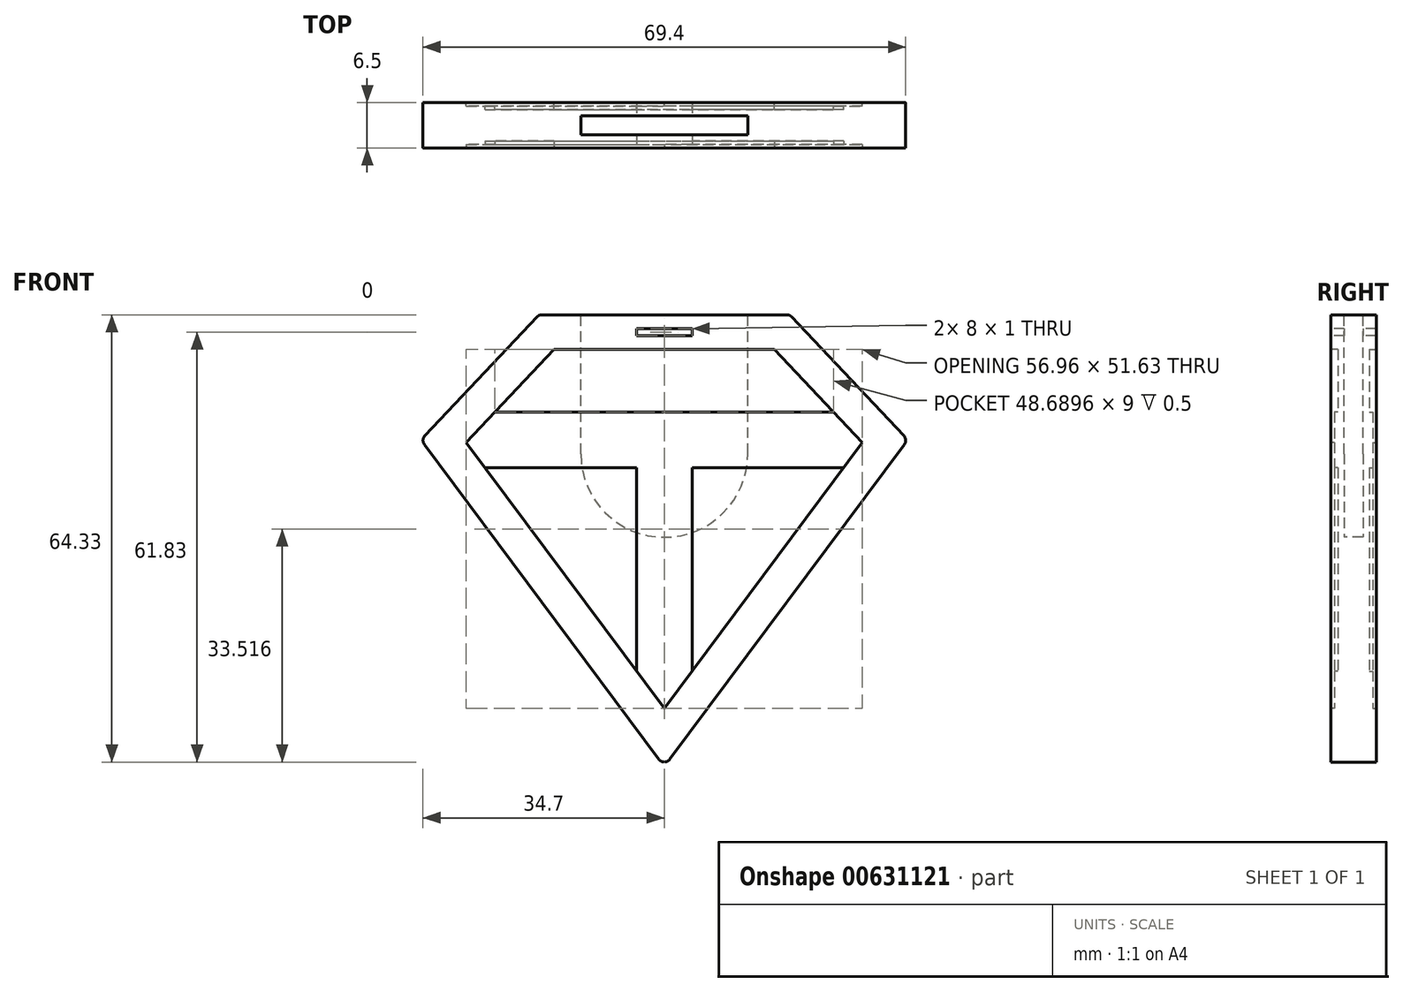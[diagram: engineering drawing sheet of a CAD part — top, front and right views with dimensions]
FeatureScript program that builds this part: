
annotation { "Feature Type Name" : "Feature", "Feature Type Description" : "" }
export const myFeature = defineFeature(function(context is Context, id is Id, definition is map)
    precondition{}
    {
        {
            var Q0;
            Q0=qCreatedBy(makeId("Front.planeOp"),FACE);
            var sketch = newSketch(context, id + "F0", { "sketchPlane" : qUnion([Q0])});
            skLineSegment(sketch, "E0", {"start": v(0, 18) * mm, "end": v(18, 18) * mm});
            skLineSegment(sketch, "E1", {"start": v(18, 18) * mm, "end": v(35, 0) * mm});
            skLineSegment(sketch, "E2", {"start": v(35, 0) * mm, "end": v(0, -47) * mm});
            skLineSegment(sketch, "E3", {"start": v(0, 18) * mm, "end": v(0, -47) * mm, "construction": true});
            skLineSegment(sketch, "E4.MirrorCS", {"start": v(-35, 0) * mm, "end": v(0, -47) * mm});
            skLineSegment(sketch, "E5.MirrorCS", {"start": v(-18, 18) * mm, "end": v(-35, 0) * mm});
            skLineSegment(sketch, "E6.MirrorCS", {"start": v(0, 18) * mm, "end": v(-18, 18) * mm});
            skSolve(sketch);
        }
        {
            var Q0;
            Q0 = qSketchRegion(id + "F0", true);
            extrude(context, id + "F1", {"entities" : qUnion([Q0]), "endBound" : BoundingType.SYMMETRIC, "depth" : 6.5 * mm, "offsetDistance" : 25 * mm});
        }
        {
            var Q0;
            Q0=makeQuery(id+"F1.opExtrude","CAP_FACE",FACE,{"disambiguationData":[OSD([sQuery(id+"F0.wireOp",EDGE,"E0"),sQuery(id+"F0.wireOp",EDGE,"E1"),sQuery(id+"F0.wireOp",EDGE,"E2"),sQuery(id+"F0.wireOp",EDGE,"E4.MirrorCS"),sQuery(id+"F0.wireOp",EDGE,"E5.MirrorCS"),sQuery(id+"F0.wireOp",EDGE,"E6.MirrorCS")])],"isStart":false});
            var sketch = newSketch(context, id + "F2", { "sketchPlane" : qUnion([Q0])});
            skLineSegment(sketch, "E7.0", {"start": v(-15.84, 13) * mm, "end": v(15.84, 13) * mm});
            skLineSegment(sketch, "E8.0", {"start": v(-15.84, 13) * mm, "end": v(-28.48, -0.38) * mm});
            skLineSegment(sketch, "E9.0", {"start": v(-28.48, -0.38) * mm, "end": v(0, -38.63) * mm});
            skLineSegment(sketch, "E10.0", {"start": v(28.48, -0.38) * mm, "end": v(0, -38.63) * mm});
            skLineSegment(sketch, "E11.0", {"start": v(15.84, 13) * mm, "end": v(28.48, -0.38) * mm});
            skSolve(sketch);
        }
        {
            var Q0;
            Q0 = qSketchRegion(id + "F2", true);
            extrude(context, id + "F3", {"entities" : qUnion([Q0]), "operationType" : NewBodyOperationType.REMOVE, "oppositeDirection" : true, "depth" : 0.5 * mm, "offsetDistance" : 25 * mm});
        }
        {
            var Q0;
            Q0=makeQuery(id+"F1.opExtrude","CAP_FACE",FACE,{"disambiguationData":[OSD([sQuery(id+"F0.wireOp",EDGE,"E0"),sQuery(id+"F0.wireOp",EDGE,"E1"),sQuery(id+"F0.wireOp",EDGE,"E2"),sQuery(id+"F0.wireOp",EDGE,"E4.MirrorCS"),sQuery(id+"F0.wireOp",EDGE,"E5.MirrorCS"),sQuery(id+"F0.wireOp",EDGE,"E6.MirrorCS")])],"isStart":true});
            var sketch = newSketch(context, id + "F4", { "sketchPlane" : qUnion([Q0])});
            skLineSegment(sketch, "E12.0", {"start": v(15.84, 13) * mm, "end": v(-15.84, 13) * mm});
            skLineSegment(sketch, "E13.0", {"start": v(15.84, 13) * mm, "end": v(28.48, -0.38) * mm});
            skLineSegment(sketch, "E14.0", {"start": v(28.48, -0.38) * mm, "end": v(0, -38.63) * mm});
            skLineSegment(sketch, "E15.0", {"start": v(-28.48, -0.38) * mm, "end": v(0, -38.63) * mm});
            skLineSegment(sketch, "E15.1", {"start": v(-15.84, 13) * mm, "end": v(-28.48, -0.38) * mm});
            skSolve(sketch);
        }
        {
            var Q0;
            Q0 = qSketchRegion(id + "F4", true);
            extrude(context, id + "F5", {"entities" : qUnion([Q0]), "operationType" : NewBodyOperationType.REMOVE, "oppositeDirection" : true, "depth" : 0.5 * mm, "offsetDistance" : 25 * mm});
        }
        {
            var Q0;
            Q0=makeQuery(id+"F3.boolean.opBoolean","COPY",FACE,{"derivedFrom":makeQuery(id+"F3.opExtrude","CAP_FACE",FACE,{"disambiguationData":[OSD([sQuery(id+"F2.wireOp",EDGE,"E7.0"),sQuery(id+"F2.wireOp",EDGE,"E8.0"),sQuery(id+"F2.wireOp",EDGE,"E9.0"),sQuery(id+"F2.wireOp",EDGE,"E10.0"),sQuery(id+"F2.wireOp",EDGE,"E11.0")])],"isStart":false})});
            var sketch = newSketch(context, id + "F6", { "sketchPlane" : qUnion([Q0])});
            skLineSegment(sketch, "E16", {"start": v(-24.34, 4) * mm, "end": v(0, 4) * mm});
            skLineSegment(sketch, "E17", {"start": v(-25.79, -4) * mm, "end": v(-4, -4) * mm});
            skLineSegment(sketch, "E18", {"start": v(-4, -4) * mm, "end": v(-4, -33.26) * mm});
            skLineSegment(sketch, "E19", {"start": v(0, 4) * mm, "end": v(0, -38.63) * mm, "construction": true});
            skLineSegment(sketch, "E20", {"start": v(-24.34, 4) * mm, "end": v(-15.84, 13) * mm});
            skLineSegment(sketch, "E21", {"start": v(-15.84, 13) * mm, "end": v(0, 13) * mm});
            skLineSegment(sketch, "E22.0", {"start": v(-25.79, -4) * mm, "end": v(-4, -33.26) * mm});
            skPoint(sketch, "E23.orphan", {"position": v(0, -38.63) * mm});
            skLineSegment(sketch, "E24.MirrorCS", {"start": v(24.34, 4) * mm, "end": v(0, 4) * mm});
            skLineSegment(sketch, "E25.MirrorCS", {"start": v(15.84, 13) * mm, "end": v(0, 13) * mm});
            skLineSegment(sketch, "E26.MirrorCS", {"start": v(25.79, -4) * mm, "end": v(4, -33.26) * mm});
            skLineSegment(sketch, "E27.MirrorCS", {"start": v(24.34, 4) * mm, "end": v(15.84, 13) * mm});
            skLineSegment(sketch, "E28.MirrorCS", {"start": v(4, -4) * mm, "end": v(4, -33.26) * mm});
            skLineSegment(sketch, "E29.MirrorCS", {"start": v(25.79, -4) * mm, "end": v(4, -4) * mm});
            skSolve(sketch);
        }
        {
            var Q0;
            Q0 = qSketchRegion(id + "F6", true);
            extrude(context, id + "F7", {"entities" : qUnion([Q0]), "operationType" : NewBodyOperationType.REMOVE, "oppositeDirection" : true, "depth" : 0.5 * mm, "offsetDistance" : 25 * mm});
        }
        {
            var Q0;
            Q0=makeQuery(id+"F5.boolean.opBoolean","COPY",FACE,{"derivedFrom":makeQuery(id+"F5.opExtrude","CAP_FACE",FACE,{"disambiguationData":[OSD([sQuery(id+"F4.wireOp",EDGE,"E12.0"),sQuery(id+"F4.wireOp",EDGE,"E13.0"),sQuery(id+"F4.wireOp",EDGE,"E14.0"),sQuery(id+"F4.wireOp",EDGE,"E15.0"),sQuery(id+"F4.wireOp",EDGE,"E15.1")])],"isStart":false})});
            var sketch = newSketch(context, id + "F8", { "sketchPlane" : qUnion([Q0])});
            skLineSegment(sketch, "E30", {"start": v(0, 13) * mm, "end": v(0, -38.63) * mm, "construction": true});
            skLineSegment(sketch, "E31", {"start": v(-24.34, 4) * mm, "end": v(0, 4) * mm});
            skLineSegment(sketch, "E32", {"start": v(-24.34, 4) * mm, "end": v(-15.84, 13) * mm});
            skLineSegment(sketch, "E33", {"start": v(-15.84, 13) * mm, "end": v(0, 13) * mm});
            skLineSegment(sketch, "E34", {"start": v(-25.79, -4) * mm, "end": v(-4, -4) * mm});
            skLineSegment(sketch, "E35", {"start": v(-4, -4) * mm, "end": v(-4, -33.26) * mm});
            skLineSegment(sketch, "E36", {"start": v(-25.79, -4) * mm, "end": v(-4, -33.26) * mm});
            skLineSegment(sketch, "E37.MirrorCS", {"start": v(25.79, -4) * mm, "end": v(4, -33.26) * mm});
            skLineSegment(sketch, "E38.MirrorCS", {"start": v(4, -4) * mm, "end": v(4, -33.26) * mm});
            skLineSegment(sketch, "E39.MirrorCS", {"start": v(25.79, -4) * mm, "end": v(4, -4) * mm});
            skLineSegment(sketch, "E40.MirrorCS", {"start": v(24.34, 4) * mm, "end": v(15.84, 13) * mm});
            skLineSegment(sketch, "E41.MirrorCS", {"start": v(15.84, 13) * mm, "end": v(0, 13) * mm});
            skLineSegment(sketch, "E42.MirrorCS", {"start": v(24.34, 4) * mm, "end": v(0, 4) * mm});
            skSolve(sketch);
        }
        {
            var Q0;
            Q0 = qSketchRegion(id + "F8", true);
            extrude(context, id + "F9", {"entities" : qUnion([Q0]), "operationType" : NewBodyOperationType.REMOVE, "oppositeDirection" : true, "depth" : 0.5 * mm, "offsetDistance" : 25 * mm});
        }
        {
            var Q0;
            Q0=makeQuery(id+"F1.opExtrude","SWEPT_FACE",FACE,{"disambiguationData":[OSD([sQuery(id+"F0.wireOp",EDGE,"E0"),sQuery(id+"F0.wireOp",EDGE,"E6.MirrorCS")])]});
            var sketch = newSketch(context, id + "F10", { "sketchPlane" : qUnion([Q0])});
            skLineSegment(sketch, "E43.bottom", {"start": v(-12, 1.35) * mm, "end": v(12, 1.35) * mm});
            skLineSegment(sketch, "E43.top", {"start": v(-12, -1.35) * mm, "end": v(12, -1.35) * mm});
            skLineSegment(sketch, "E43.left", {"start": v(-12, 1.35) * mm, "end": v(-12, -1.35) * mm});
            skLineSegment(sketch, "E43.right", {"start": v(12, 1.35) * mm, "end": v(12, -1.35) * mm});
            skSolve(sketch);
        }
        {
            var Q0;
            Q0 = qSketchRegion(id + "F10", true);
            extrude(context, id + "F11", {"entities" : qUnion([Q0]), "operationType" : NewBodyOperationType.REMOVE, "oppositeDirection" : true, "depth" : 20 * mm, "offsetDistance" : 25 * mm});
        }
        {
            var Q0;
            Q0=qCreatedBy(makeId("Front.planeOp"),FACE);
            var sketch = newSketch(context, id + "F12", { "sketchPlane" : qUnion([Q0])});
            skLineSegment(sketch, "E44.0", {"start": v(-12, -2) * mm, "end": v(12, -2) * mm});
            skArc(sketch, "E45", {"start": v(-12, -2) * mm, "mid": v(0, -14) * mm, "end": v(12, -2) * mm});
            skSolve(sketch);
        }
        {
            var Q0;
            Q0 = qSketchRegion(id + "F12", true);
            extrude(context, id + "F13", {"entities" : qUnion([Q0]), "operationType" : NewBodyOperationType.REMOVE, "endBound" : BoundingType.SYMMETRIC, "oppositeDirection" : true, "depth" : 2.7 * mm, "offsetDistance" : 25 * mm});
        }
        {
            var Q0;
            Q0=makeQuery(id+"F1.opExtrude","CAP_FACE",FACE,{"disambiguationData":[OSD([sQuery(id+"F0.wireOp",EDGE,"E0"),sQuery(id+"F0.wireOp",EDGE,"E1"),sQuery(id+"F0.wireOp",EDGE,"E2"),sQuery(id+"F0.wireOp",EDGE,"E4.MirrorCS"),sQuery(id+"F0.wireOp",EDGE,"E5.MirrorCS"),sQuery(id+"F0.wireOp",EDGE,"E6.MirrorCS")])],"isStart":false});
            var sketch = newSketch(context, id + "F14", { "sketchPlane" : qUnion([Q0])});
            skLineSegment(sketch, "E46.bottom", {"start": v(-4, 16) * mm, "end": v(4, 16) * mm});
            skLineSegment(sketch, "E46.top", {"start": v(-4, 15) * mm, "end": v(4, 15) * mm});
            skLineSegment(sketch, "E46.left", {"start": v(-4, 16) * mm, "end": v(-4, 15) * mm});
            skLineSegment(sketch, "E46.right", {"start": v(4, 16) * mm, "end": v(4, 15) * mm});
            skSolve(sketch);
        }
        {
            var Q0;
            Q0 = qSketchRegion(id + "F14", true);
            extrude(context, id + "F15", {"entities" : qUnion([Q0]), "operationType" : NewBodyOperationType.REMOVE, "oppositeDirection" : true, "depth" : 25 * mm, "offsetDistance" : 25 * mm});
        }
        {
            var Q0;
            Q0=makeQuery(id+"F1.opExtrude","SWEPT_EDGE",EDGE,{"disambiguationData":[OSD([sQuery(id+"F0.wireOp",EDGE,"E2"),sQuery(id+"F0.wireOp",EDGE,"E4.MirrorCS")])]});
            var Q1;
            Q1=makeQuery(id+"F1.opExtrude","SWEPT_EDGE",EDGE,{"disambiguationData":[OSD([sQuery(id+"F0.wireOp",EDGE,"E1"),sQuery(id+"F0.wireOp",EDGE,"E2")])]});
            var Q2;
            Q2=makeQuery(id+"F1.opExtrude","SWEPT_EDGE",EDGE,{"disambiguationData":[OSD([sQuery(id+"F0.wireOp",EDGE,"E4.MirrorCS"),sQuery(id+"F0.wireOp",EDGE,"E5.MirrorCS")])]});
            var Q3;
            Q3=makeQuery(id+"F1.opExtrude","SWEPT_EDGE",EDGE,{"disambiguationData":[OSD([sQuery(id+"F0.wireOp",EDGE,"E5.MirrorCS"),sQuery(id+"F0.wireOp",EDGE,"E6.MirrorCS")])]});
            var Q4;
            Q4=makeQuery(id+"F1.opExtrude","SWEPT_EDGE",EDGE,{"disambiguationData":[OSD([sQuery(id+"F0.wireOp",EDGE,"E0"),sQuery(id+"F0.wireOp",EDGE,"E1")])]});
            fillet(context, id + "F16", {"entities" : qUnion([Q0, Q1, Q2, Q3, Q4]), "radius" : 1 * mm, "tangentPropagation" : true, "allowEdgeOverflow" : false});
        }
    });
